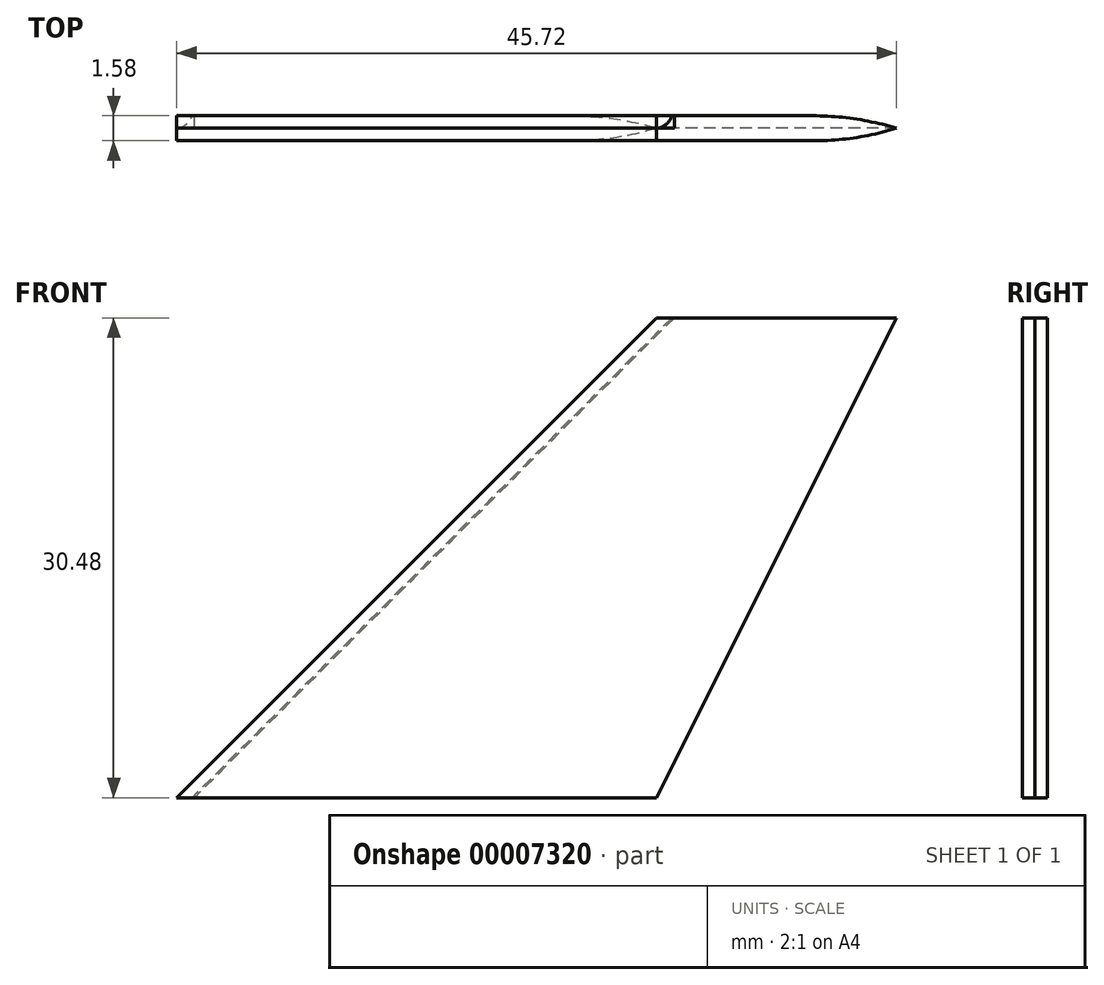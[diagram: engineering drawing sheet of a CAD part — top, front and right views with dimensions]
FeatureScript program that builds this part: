
annotation { "Feature Type Name" : "Feature", "Feature Type Description" : "" }
export const myFeature = defineFeature(function(context is Context, id is Id, definition is map)
    precondition{}
    {
        {
            var Q0;
            Q0=qCreatedBy(makeId("Front.planeOp"),FACE);
            var sketch = newSketch(context, id + "F0", { "sketchPlane" : qUnion([Q0])});
            skLineSegment(sketch, "E0", {"start": v(0, 0) * mm, "end": v(30.48, 30.48) * mm});
            skLineSegment(sketch, "E1", {"start": v(30.48, 30.48) * mm, "end": v(45.72, 30.48) * mm});
            skLineSegment(sketch, "E2", {"start": v(45.72, 30.48) * mm, "end": v(30.48, 0) * mm});
            skLineSegment(sketch, "E3", {"start": v(30.48, 0) * mm, "end": v(0, 0) * mm});
            skSolve(sketch);
        }
        {
            var Q0;
            Q0=makeQuery(id+"F0.imprint","IMPRINT",FACE,{"disambiguationData":[TD([[makeQuery(id+"F0.imprint","IMPRINT",EDGE,{"derivedFrom":sQuery(id+"F0.wireOp",EDGE,"E0")}),-1.0]])]});
            extrude(context, id + "F1", {"entities" : qUnion([Q0]), "depth" : 1.59 * mm, "symmetric" : true});
        }
        {
            var Q0;
            Q0=sQuery(id+"F0.wireOp",EDGE,"E0");
            var Q1;
            Q1=sQuery(id+"F0.wireOp",VERTEX,"E3.end");
            cPlane(context, id + "F2", {"entities" : qUnion([Q0, Q1]), "cplaneType" : CPlaneType.CURVE_POINT, "offset" : 152.4 * mm, "width" : 152.4 * mm, "height" : 152.4 * mm});
        }
        {
            var Q0;
            Q0=qCreatedBy(id+"F2.planeOp",FACE);
            var sketch = newSketch(context, id + "F3", { "sketchPlane" : qUnion([Q0])});
            skLineSegment(sketch, "E4.0", {"start": v(0, 0.8) * mm, "end": v(10.78, 0.8) * mm});
            skLineSegment(sketch, "E4.1", {"start": v(0, -0.8) * mm, "end": v(10.78, -0.8) * mm});
            skLineSegment(sketch, "E4.2", {"start": v(0, -0.8) * mm, "end": v(0, 0.8) * mm});
            skLineSegment(sketch, "E5.0", {"start": v(21.55, 0) * mm, "end": v(0, 0) * mm, "construction": true});
            skCircle(sketch, "E6", {"center": v(0.8, 0) * mm, "radius": 0.8 * mm, "construction": true});
            skLineSegment(sketch, "E7", {"start": v(1.59, 0.8) * mm, "end": v(1.59, -0.8) * mm});
            skEllipticalArc(sketch, "E8", {});
            skLineSegment(sketch, "E9", {"start": v(1.59, 0.8) * mm, "end": v(1.59, 3.33) * mm});
            skLineSegment(sketch, "E10", {"start": v(1.59, 3.33) * mm, "end": v(-2.54, 3.33) * mm});
            skLineSegment(sketch, "E11", {"start": v(-2.54, 3.33) * mm, "end": v(-2.54, -3.33) * mm});
            skLineSegment(sketch, "E12", {"start": v(-2.54, -3.33) * mm, "end": v(1.59, -3.33) * mm});
            skLineSegment(sketch, "E13", {"start": v(1.59, -3.33) * mm, "end": v(1.59, -0.8) * mm});
            const initialGuessF3  = {"E8": [0.0015874999999999978, 0, -1, 0, 0.0015874999999999978, 0.0007937500000000001, 4.71238898038469, 1.5707963267948966]};
            skSetInitialGuess(sketch, initialGuessF3);
            skSolve(sketch);
        }
        {
            var Q0;
            {var subQ0=sQuery(id+"F3.wireOp",EDGE,"E9");Q0=makeQuery(id+"F3.imprint","IMPRINT",FACE,{"disambiguationData":[TD([[makeQuery(id+"F3.imprint","IMPRINT",EDGE,{"derivedFrom":subQ0}),1.0]])]});}
            var Q1;
            {var subQ1=sQuery(id+"F3.wireOp",EDGE,"E4.2");var subQ3=sQuery(id+"F3.wireOp",EDGE,"E4.1");var subQ5=makeQuery(id+"F3.imprint","INTERSECT",VERTEX,{"derivedFrom":[subQ3,subQ1]});Q1=makeQuery(id+"F3.imprint","IMPRINT",FACE,{"disambiguationData":[TD([[makeQuery(id+"F3.imprint","IMPRINT",EDGE,{"disambiguationData":[TD([[subQ5,-1.0]])],"derivedFrom":subQ1}),-1.0]])]});}
            var Q2;
            {var subQ1=sQuery(id+"F3.wireOp",EDGE,"E4.2");var subQ3=sQuery(id+"F3.wireOp",EDGE,"E4.0");var subQ5=makeQuery(id+"F3.imprint","INTERSECT",VERTEX,{"derivedFrom":[subQ3,subQ1]});Q2=makeQuery(id+"F3.imprint","IMPRINT",FACE,{"disambiguationData":[TD([[makeQuery(id+"F3.imprint","IMPRINT",EDGE,{"disambiguationData":[TD([[subQ5,1.0]])],"derivedFrom":subQ1}),-1.0]])]});}
            extrude(context, id + "F4", {"entities" : qUnion([Q0, Q1, Q2]), "operationType" : NewBodyOperationType.REMOVE, "endBound" : BoundingType.THROUGH_ALL, "depth" : 25.4 * mm});
        }
        {
            var Q0;
            Q0=sQuery(id+"F0.wireOp",EDGE,"E2");
            var Q1;
            Q1=sQuery(id+"F0.wireOp",VERTEX,"E3.start");
            cPlane(context, id + "F5", {"entities" : qUnion([Q0, Q1]), "cplaneType" : CPlaneType.CURVE_POINT, "offset" : 152.4 * mm, "width" : 152.4 * mm, "height" : 152.4 * mm});
        }
        {
            var Q0;
            Q0=qCreatedBy(id+"F5.planeOp",FACE);
            var sketch = newSketch(context, id + "F6", { "sketchPlane" : qUnion([Q0])});
            skLineSegment(sketch, "E14.0", {"start": v(24.09, -0.8) * mm, "end": v(27.26, -0.8) * mm, "construction": true});
            skLineSegment(sketch, "E14.1", {"start": v(27.26, 0.8) * mm, "end": v(27.26, -0.8) * mm, "construction": true});
            skLineSegment(sketch, "E14.2", {"start": v(24.09, 0.8) * mm, "end": v(27.26, 0.8) * mm, "construction": true});
            skLineSegment(sketch, "E14.3", {"start": v(27.26, 0) * mm, "end": v(0, 0) * mm, "construction": true});
            skCircle(sketch, "E15", {"center": v(26.47, 0) * mm, "radius": 0.8 * mm, "construction": true});
            skCircle(sketch, "E16", {"center": v(24.88, 0) * mm, "radius": 0.8 * mm, "construction": true});
            skLineSegment(sketch, "E17", {"start": v(24.09, -0.8) * mm, "end": v(24.09, 0.8) * mm, "construction": true});
            skLineSegment(sketch, "E18", {"start": v(24.09, -0.8) * mm, "end": v(22.5, -0.8) * mm, "construction": true});
            skPoint(sketch, "E18.endSnap0", {"position": v(13.63, 0) * mm});
            skArc(sketch, "E19", {"start": v(24.09, -0.8) * mm, "mid": v(25.72, -0.6) * mm, "end": v(27.26, 0) * mm, "construction": true});
            skCircle(sketch, "E20", {"center": v(23.3, 0) * mm, "radius": 0.8 * mm, "construction": true});
            skLineSegment(sketch, "E21", {"start": v(24.09, 0.8) * mm, "end": v(13.63, 0.8) * mm, "construction": true});
            skLineSegment(sketch, "E22", {"start": v(22.5, -0.8) * mm, "end": v(22.5, 0.8) * mm, "construction": true});
            skLineSegment(sketch, "E23", {"start": v(22.5, -0.8) * mm, "end": v(13.63, -0.8) * mm});
            skLineSegment(sketch, "E24", {"start": v(13.63, -0.8) * mm, "end": v(13.63, 0.8) * mm});
            skArc(sketch, "E25", {"start": v(22.5, -0.8) * mm, "mid": v(24.91, -0.6) * mm, "end": v(27.26, 0) * mm});
            skLineSegment(sketch, "E26", {"start": v(22.5, -0.8) * mm, "end": v(22.5, -3.33) * mm});
            skLineSegment(sketch, "E27", {"start": v(22.5, -3.33) * mm, "end": v(29.8, -3.33) * mm});
            skLineSegment(sketch, "E28", {"start": v(29.8, -3.33) * mm, "end": v(29.8, 3.33) * mm});
            skLineSegment(sketch, "E29", {"start": v(29.8, 3.33) * mm, "end": v(22.5, 3.33) * mm});
            skLineSegment(sketch, "E30", {"start": v(22.5, 3.33) * mm, "end": v(22.5, 0.8) * mm});
            skArc(sketch, "E31.MirrorCS", {"start": v(22.5, 0.8) * mm, "mid": v(24.91, 0.6) * mm, "end": v(27.26, 0) * mm});
            skSolve(sketch);
        }
        {
            var Q0;
            Q0=makeQuery(id+"F6.imprint","IMPRINT",FACE,{"disambiguationData":[TD([[makeQuery(id+"F6.imprint","IMPRINT",EDGE,{"derivedFrom":sQuery(id+"F6.wireOp",EDGE,"E25")}),-1.0]])]});
            extrude(context, id + "F7", {"entities" : qUnion([Q0]), "operationType" : NewBodyOperationType.REMOVE, "oppositeDirection" : true, "depth" : 127 * mm, "symmetric" : true});
        }
    });
